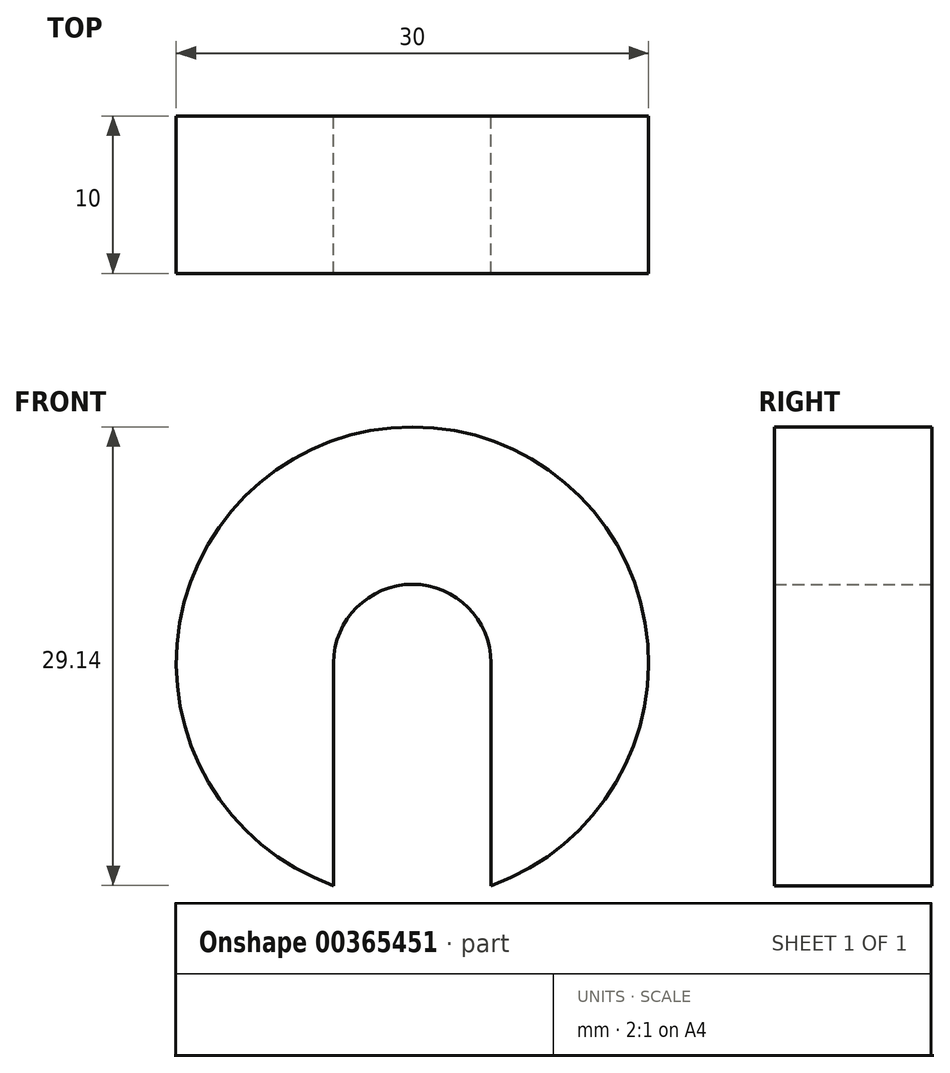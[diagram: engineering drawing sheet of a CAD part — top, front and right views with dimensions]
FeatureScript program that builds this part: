
annotation { "Feature Type Name" : "Feature", "Feature Type Description" : "" }
export const myFeature = defineFeature(function(context is Context, id is Id, definition is map)
    precondition{}
    {
        {
            var Q0;
            Q0=qCreatedBy(makeId("Front.planeOp"),FACE);
            var sketch = newSketch(context, id + "F0", { "sketchPlane" : qUnion([Q0])});
            skArc(sketch, "E0", {"start": v(5, -14.14) * mm, "mid": v(0, 15) * mm, "end": v(-5, -14.14) * mm});
            skArc(sketch, "E1", {"start": v(5, 0) * mm, "mid": v(0, 5) * mm, "end": v(-5, 0) * mm});
            skLineSegment(sketch, "E2", {"start": v(5, 0) * mm, "end": v(5, -14.14) * mm});
            skLineSegment(sketch, "E3", {"start": v(-5, 0) * mm, "end": v(-5, -14.14) * mm});
            skSolve(sketch);
        }
        {
            var Q0;
            Q0=makeQuery(id+"F0.imprint","IMPRINT",FACE,{"disambiguationData":[TD([[makeQuery(id+"F0.imprint","IMPRINT",EDGE,{"derivedFrom":sQuery(id+"F0.wireOp",EDGE,"E0")}),1.0]])]});
            extrude(context, id + "F1", {"entities" : qUnion([Q0]), "depth" : 10 * mm});
        }
    });
